# Revit family: Door_Bi-parting_UltiGroup_Flex
name_source: partatom
category: Doors
units: mm (PartAtom-declared; Revit-internal decimal feet)

## family parameters
Always vertical = Yes
Cut with Voids When Loaded = No
Host = Wall
OmniClass Number = 23.30.10.21.17.11
OmniClass Title = Cold Storage Doors
Room Calculation Point = No
Shared = No

## types (1)
- Type 1
    Analytic Construction = <None>
    Bottom Door Height = 40 mm  [stored 0.131234 ft]
    Conduit = Conduit
    Control Box distance = 100 mm  [stored 0.328084 ft]
    Control Box height = 1300 mm  [stored 4.26509 ft]
    Define Thermal Properties by = Schematic Type
    Description = Ulti Flex Door - Bi Parting
    Door Frame Depth = 40 mm  [stored 0.131234 ft]
    Door Frame Width = 100 mm  [stored 0.328084 ft]
    Door Handle height = 1000 mm  [stored 3.28084 ft]
    Door Leaf distance from wall = 70 mm  [stored 0.229659 ft]
    Door Open = 0 mm  [stored 0 ft]
    Door Seals = Door Seals
    DoorFrameMaterial_ANZRS = Door Frame Material
    DoorGlazingHeight_ANZRS = 4825 mm
    DoorGlazingWidth_ANZRS = 0 mm  [stored 0 ft]
    DoorGrilleHeight_ANZRS = 0 mm  [stored 0 ft]
    DoorGrilleWidth_ANZRS = 0 mm  [stored 0 ft]
    DoorGrille_ANZRS = No
    DoorNumberOfPanels_ANZRS = 0
    DoorOperation_ANZRS = [OPEN-CLOSE push button][Double through photo beam eyes][Emergency manual handle]
    DoorPanelBWidth_ANZRS = 1550 mm  [stored 5.0853 ft]
    DoorPanelDepth_ANZRS = 150 mm  [stored 0.492126 ft]
    DoorPanelFinish_ANZRS = Reinforced PVC Curtain
    DoorPanelHeight_ANZRS = 3150 mm  [stored 10.3346 ft]
    DoorPanelMaterial_ANZRS = Door Panel Material
    DoorPanelWidth_ANZRS = 1610 mm  [stored 5.28215 ft]
    Fax = 07 846 2467
    Function = Interior
    Guide = Guide
    Height = 3000 mm  [stored 9.84252 ft]
    InstallationGroup_ANZRS = 0
    Manufacturer = Ulti Group Ltd.
    Model = Ulti Flex Door
    ModifiedIssue_ANZRS = 0 $
    Overhead Hood Cover = Yes
    Overhead Hood finish = Overhead Hood
    Send Message = http://ultigroup.co.nz
    Steel Black = Steel Black
    Top Hood Length = 6450 mm  [stored 21.1614 ft]
    URL = www.ultigroup.co.nz
    Wall Closure = By host
    Width = 3000 mm  [stored 9.84252 ft]

note: [stored X ft] marks values corroborated as IEEE doubles in the binary element streams (Revit-internal decimal feet)

## geometry (parser evidence)
native form markers: Blend x2, Sweep x27
no freeform markers — native parametric forms only
